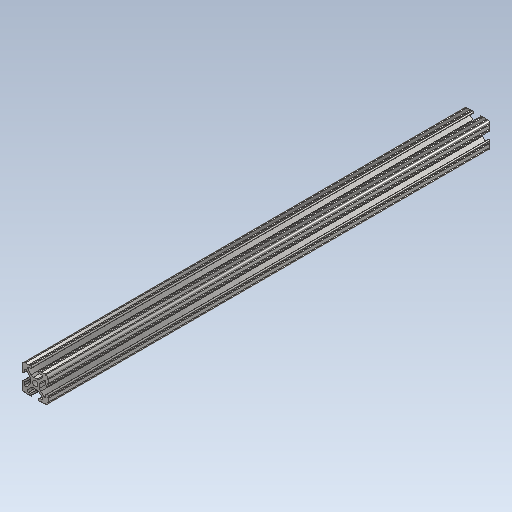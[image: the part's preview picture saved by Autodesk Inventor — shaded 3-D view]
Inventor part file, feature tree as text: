
AUTODESK INVENTOR PART (.ipt)
format: ipt  version: 2020 (Build 240168000, 168)  size: 248,832 bytes
history: native  units: in
note: dims shown in document units (in); Inventor stores cm internally (conversion verified against a paired STEP export)
features: extrude x1, sketch x1
ambient origin geometry x8: Origin, YZ Plane, XZ Plane, XY Plane, X Axis, Y Axis, Z Axis, Center Point
bodies: Solid1 (feature_tree)
feature tree (2):
  extrude  "Extrusion1"  [1 undecoded]
  sketch  "Sketch1"  dims[d0=17.0in d1=0.0in]
note: 1 required parameter value undecoded (feature->parameter linkage not recoverable at this tier; creation-order binding heuristic only, values carry confidence <= 0.55)
